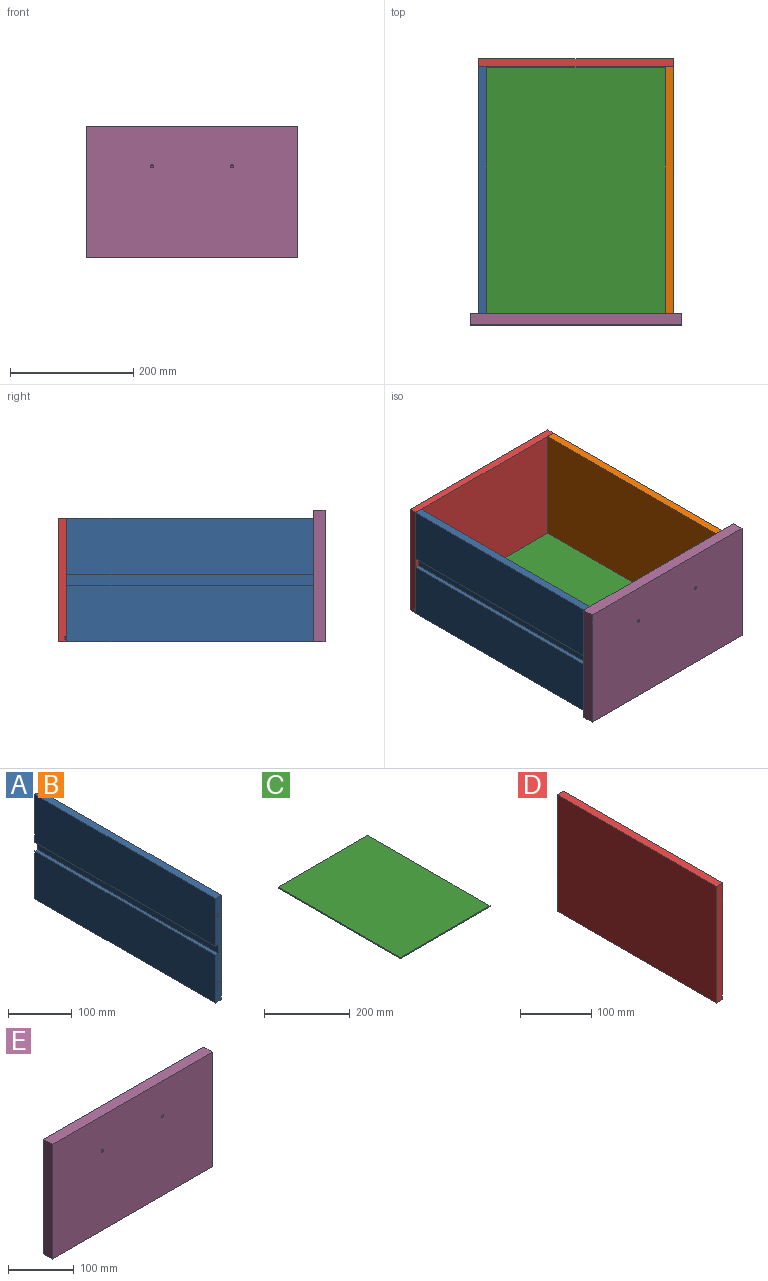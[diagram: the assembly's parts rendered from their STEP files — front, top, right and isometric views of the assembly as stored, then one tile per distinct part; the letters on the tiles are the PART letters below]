
ASSEMBLY  parts=5 mates=4
PART A: 22 faces, bbox 13x400x200 mm
  f0: plane 400x4mm, normal (1,0,0), area 1600mm2, adj f1,f11,f12,f13
  f1: plane 400x3.62mm, normal (0,0,1), area 1447.1mm2, adj f0,f2,f12,f13
  f2: plane 400x4mm, normal (1,0,0), area 1600mm2, adj f1,f3,f12,f13
  f3: plane 400x3.62mm, normal (0,0,-1), area 1447.1mm2, adj f2,f4,f12,f13
  f4: plane 400x192mm, normal (1,0,0), area 76800mm2, adj f3,f5,f12,f13
  f5: plane 400x13mm, normal (0,0,1), area 5200mm2, adj f4,f6,f12,f13
  f6: plane 400x91.5mm, normal (-1,0,0), area 36600mm2, adj f5,f7,f12,f13
  f7: plane 400x6mm, normal (0,0,-1), area 2400mm2, adj f6,f8,f12,f13
  f8: plane 400x17mm, normal (-1,0,0), area 6800mm2, adj f7,f9,f12,f13
  f9: plane 400x6mm, normal (0,0,1), area 2400mm2, adj f8,f10,f12,f13
  f10: plane 400x91.5mm, normal (-1,0,0), area 36600mm2, adj f9,f11,f12,f13
  f11: plane 400x13mm, normal (0,0,-1), area 5200mm2, adj f0,f10,f12,f13
  f12: plane 200x13mm, normal (0,1,0), area 2427mm2, adj f0,f1,f2,f3,f4,f5,f6,f7
  f13: plane 200x13mm, normal (0,-1,0), area 2427mm2, adj f0,f1,f2,f3,f4,f5,f6,f7
  f14: cylinder r=3mm len=15mm, axis (0,-1,0), area 282.7mm2, adj f13,f15
  f15: cone r=0mm half-angle=59deg, axis (0,-1,0), area 33mm2, adj f14
  f16: cylinder r=3mm len=15mm, axis (0,-1,0), area 282.7mm2, adj f13,f17
  f17: cone r=0mm half-angle=59deg, axis (0,-1,0), area 33mm2, adj f16
  f18: cylinder r=3mm len=15mm, axis (0,1,0), area 282.7mm2, adj f12,f19
  f19: cone r=0mm half-angle=59deg, axis (0,1,0), area 33mm2, adj f18
  f20: cylinder r=3mm len=15mm, axis (0,1,0), area 282.7mm2, adj f12,f21
  f21: cone r=0mm half-angle=59deg, axis (0,1,0), area 33mm2, adj f20
PART B: same geometry as A
PART C: 6 faces, bbox 297x404x3 mm
  f0: plane 404x3mm, normal (-1,0,0), area 1212mm2, adj f1,f3,f4,f5
  f1: plane 297x3mm, normal (0,-1,0), area 891mm2, adj f0,f2,f4,f5
  f2: plane 404x3mm, normal (1,0,0), area 1212mm2, adj f1,f3,f4,f5
  f3: plane 297x3mm, normal (0,1,0), area 891mm2, adj f0,f2,f4,f5
  f4: plane 404x297mm, normal (0,0,1), area 119988mm2, adj f0,f1,f2,f3
  f5: plane 404x297mm, normal (0,0,-1), area 119988mm2, adj f0,f1,f2,f3
PART D: 18 faces, bbox 13x316x200 mm
  f0: plane 316x4mm, normal (1,0,0), area 1264mm2, adj f1,f7,f8,f9
  f1: plane 316x3.62mm, normal (0,0,1), area 1143.2mm2, adj f0,f2,f8,f9
  f2: plane 316x4mm, normal (1,0,0), area 1264mm2, adj f1,f3,f8,f9
  f3: plane 316x3.62mm, normal (0,0,-1), area 1143.2mm2, adj f2,f4,f8,f9
  f4: plane 316x192mm, normal (1,0,0), area 60558.9mm2, adj f3,f5,f8,f9,f10,f12,f14,f16
  f5: plane 316x13mm, normal (0,0,1), area 4108mm2, adj f4,f6,f8,f9
  f6: plane 316x200mm, normal (-1,0,0), area 63200mm2, adj f5,f7,f8,f9
  f7: plane 316x13mm, normal (0,0,-1), area 4108mm2, adj f0,f6,f8,f9
  f8: plane 200x13mm, normal (0,1,0), area 2585.5mm2, adj f0,f1,f2,f3,f4,f5,f6,f7
  f9: plane 200x13mm, normal (0,-1,0), area 2585.5mm2, adj f0,f1,f2,f3,f4,f5,f6,f7
  f10: cylinder r=3mm len=10mm, axis (1,0,0), area 188.5mm2, adj f4,f11
  f11: cone r=0mm half-angle=59deg, axis (1,0,0), area 33mm2, adj f10
  f12: cylinder r=3mm len=10mm, axis (1,0,0), area 188.5mm2, adj f4,f13
  f13: cone r=0mm half-angle=59deg, axis (1,0,0), area 33mm2, adj f12
  f14: cylinder r=3mm len=10mm, axis (1,0,0), area 188.5mm2, adj f4,f15
  f15: cone r=0mm half-angle=59deg, axis (1,0,0), area 33mm2, adj f14
  f16: cylinder r=3mm len=10mm, axis (1,0,0), area 188.5mm2, adj f4,f17
  f17: cone r=0mm half-angle=59deg, axis (1,0,0), area 33mm2, adj f16
PART E: 16 faces, bbox 344x19x213 mm
  f0: plane 213x19mm, normal (-1,0,0), area 4047mm2, adj f1,f3,f4,f5
  f1: plane 344x19mm, normal (0,0,-1), area 6536mm2, adj f0,f2,f4,f5
  f2: plane 213x19mm, normal (1,0,0), area 4047mm2, adj f1,f3,f4,f5
  f3: plane 344x19mm, normal (0,0,1), area 6536mm2, adj f0,f2,f4,f5
  f4: plane 344x213mm, normal (0,-1,0), area 73232.7mm2, adj f0,f1,f2,f3,f14,f15
  f5: plane 344x213mm, normal (0,1,0), area 73119.6mm2, adj f0,f1,f2,f3,f6,f8,f10,f12
  f6: cylinder r=3mm len=15mm, axis (0,1,0), area 282.7mm2, adj f5,f7
  f7: cone r=0mm half-angle=59deg, axis (0,1,0), area 33mm2, adj f6
  f8: cylinder r=3mm len=15mm, axis (0,1,0), area 282.7mm2, adj f5,f9
  f9: cone r=0mm half-angle=59deg, axis (0,1,0), area 33mm2, adj f8
  f10: cylinder r=3mm len=15mm, axis (0,1,0), area 282.7mm2, adj f5,f11
  f11: cone r=0mm half-angle=59deg, axis (0,1,0), area 33mm2, adj f10
  f12: cylinder r=3mm len=15mm, axis (0,1,0), area 282.7mm2, adj f5,f13
  f13: cone r=0mm half-angle=59deg, axis (0,1,0), area 33mm2, adj f12
  f14: cylinder r=2.5mm len=19mm, axis (0,-1,0), area 298.5mm2, adj f4,f5
  f15: cylinder r=2.5mm len=19mm, axis (0,-1,0), area 298.5mm2, adj f4,f5
PLACE A t=(-210.38,183.04,4.8)mm
PLACE B rot(axis=(0,0,1),180deg) t=(92.62,183.04,4.8)mm
PLACE C t=(-58.77,185.04,-89.2)mm
PLACE D rot(axis=(0,0,-1),90deg) t=(-58.88,389.54,4.8)mm
PLACE E t=(-58.88,-16.96,11.3)mm fixed
MATE fastened B.f14 <-> E.f6  axis (0,-1,0) through (92.62,-16.96,69.8)mm
MATE fastened A.f16 <-> E.f12  axis (0,-1,0) through (-210.38,-16.96,-60.2)mm
MATE fastened B.f14 <-> D.f14  axis (0,1,0) through (92.62,383.04,69.8)mm
MATE fastened B.f2 <-> C.f2  axis (-1,0,0) through (89.73,183.04,-89.2)mm
